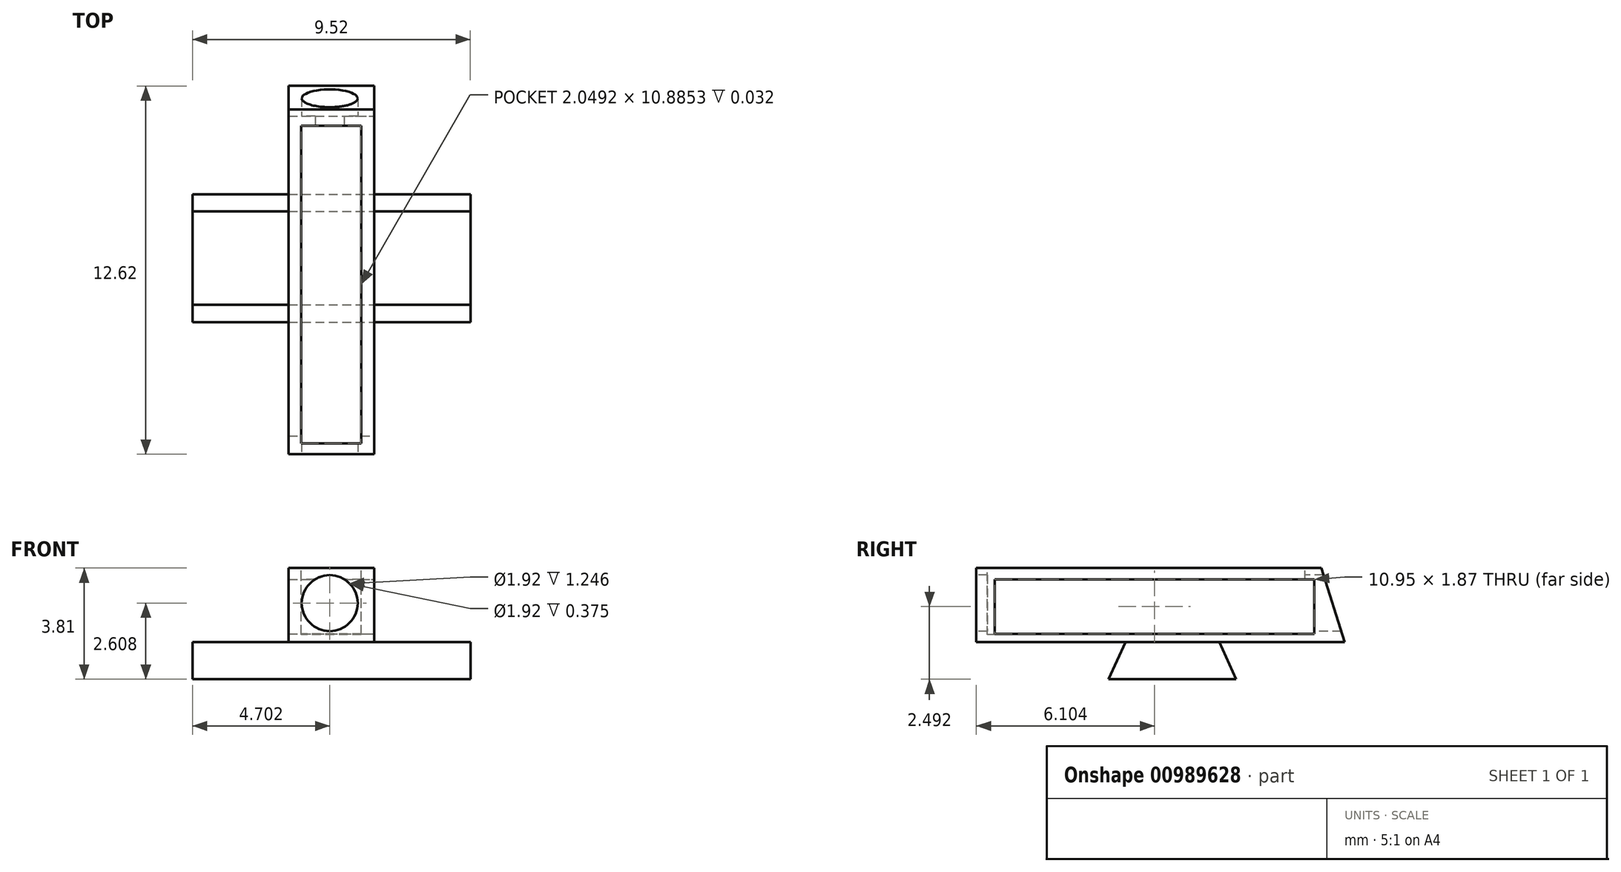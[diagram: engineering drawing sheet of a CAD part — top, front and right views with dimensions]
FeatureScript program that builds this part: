
annotation { "Feature Type Name" : "Feature", "Feature Type Description" : "" }
export const myFeature = defineFeature(function(context is Context, id is Id, definition is map)
    precondition{}
    {
        {
            var Q0;
            Q0=qCreatedBy(makeId("Top.planeOp"),FACE);
            var sketch = newSketch(context, id + "F0", { "sketchPlane" : qUnion([Q0])});
            skLineSegment(sketch, "E0.bottom", {"start": v(-27.98, 8.9) * mm, "end": v(-18.46, 8.9) * mm});
            skLineSegment(sketch, "E0.top", {"start": v(-27.98, 4.52) * mm, "end": v(-18.46, 4.52) * mm});
            skLineSegment(sketch, "E0.left", {"start": v(-27.98, 8.9) * mm, "end": v(-27.98, 4.52) * mm});
            skLineSegment(sketch, "E0.right", {"start": v(-18.46, 8.9) * mm, "end": v(-18.46, 4.52) * mm});
            skSolve(sketch);
        }
        {
            var Q0;
            Q0 = qSketchRegion(id + "F0", true);
            extrude(context, id + "F1", {"entities" : qUnion([Q0]), "depth" : 1.27 * mm, "offsetDistance" : 25.4 * mm});
        }
        {
            var Q0;
            Q0=makeQuery(id+"F1.opExtrude","CAP_FACE",FACE,{"disambiguationData":[OSD([sQuery(id+"F0.wireOp",EDGE,"E0.bottom"),sQuery(id+"F0.wireOp",EDGE,"E0.top"),sQuery(id+"F0.wireOp",EDGE,"E0.left"),sQuery(id+"F0.wireOp",EDGE,"E0.right")])],"isStart":false});
            var sketch = newSketch(context, id + "F2", { "sketchPlane" : qUnion([Q0])});
            skLineSegment(sketch, "E1.bottom", {"start": v(-21.75, 0) * mm, "end": v(-24.69, 0) * mm});
            skLineSegment(sketch, "E1.top", {"start": v(-21.75, 12.62) * mm, "end": v(-24.69, 12.62) * mm});
            skLineSegment(sketch, "E1.left", {"start": v(-21.75, 0) * mm, "end": v(-21.75, 12.62) * mm});
            skLineSegment(sketch, "E1.right", {"start": v(-24.69, 0) * mm, "end": v(-24.69, 12.62) * mm});
            skSolve(sketch);
        }
        {
            var Q0;
            Q0 = qSketchRegion(id + "F2", true);
            extrude(context, id + "F3", {"entities" : qUnion([Q0]), "operationType" : NewBodyOperationType.ADD, "depth" : 2.54 * mm, "offsetDistance" : 25.4 * mm});
        }
        {
            var Q0;
            Q0=makeQuery(id+"F3.opExtrude","SWEPT_FACE",FACE,{"disambiguationData":[OSD([sQuery(id+"F2.wireOp",EDGE,"E1.bottom")])]});
            var sketch = newSketch(context, id + "F4", { "sketchPlane" : qUnion([Q0])});
            skSolve(sketch);
        }
        {
            var Q0;
            Q0=makeQuery(id+"F1.opExtrude","SWEPT_FACE",FACE,{"disambiguationData":[OSD([sQuery(id+"F0.wireOp",EDGE,"E0.right")])]});
            var sketch = newSketch(context, id + "F5", { "sketchPlane" : qUnion([Q0])});
            skLineSegment(sketch, "E2", {"start": v(8.9, 0) * mm, "end": v(8.32, 1.27) * mm});
            skLineSegment(sketch, "E3", {"start": v(4.52, 0) * mm, "end": v(5.12, 1.27) * mm});
            skSolve(sketch);
        }
        {
            var Q0;
            {var subQ0=sQuery(id+"F5.wireOp",EDGE,"E3");Q0=makeQuery(id+"F5.imprint","IMPRINT",FACE,{"disambiguationData":[TD([[makeQuery(id+"F5.imprint","IMPRINT",EDGE,{"derivedFrom":subQ0}),1.0]])]});}
            var Q1;
            {var subQ0=sQuery(id+"F5.wireOp",EDGE,"E2");Q1=makeQuery(id+"F5.imprint","IMPRINT",FACE,{"disambiguationData":[TD([[makeQuery(id+"F5.imprint","IMPRINT",EDGE,{"derivedFrom":subQ0}),-1.0]])]});}
            extrude(context, id + "F6", {"entities" : qUnion([Q0, Q1]), "operationType" : NewBodyOperationType.REMOVE, "oppositeDirection" : true, "depth" : 25.4 * mm, "offsetDistance" : 25.4 * mm});
        }
        {
            var Q0;
            Q0=makeQuery(id+"F3.opExtrude","SWEPT_FACE",FACE,{"disambiguationData":[OSD([sQuery(id+"F2.wireOp",EDGE,"E1.left")])]});
            var sketch = newSketch(context, id + "F7", { "sketchPlane" : qUnion([Q0])});
            skLineSegment(sketch, "E4", {"start": v(12.62, 1.27) * mm, "end": v(11.82, 3.81) * mm});
            skLineSegment(sketch, "E5.bottom", {"start": v(1.04, 3.3) * mm, "end": v(11.61, 3.3) * mm});
            skLineSegment(sketch, "E5.top", {"start": v(1.04, 1.8) * mm, "end": v(11.61, 1.8) * mm});
            skLineSegment(sketch, "E5.left", {"start": v(1.04, 3.3) * mm, "end": v(1.04, 1.8) * mm});
            skLineSegment(sketch, "E5.right", {"start": v(11.61, 3.3) * mm, "end": v(11.61, 1.8) * mm});
            skSolve(sketch);
        }
        {
            var Q0;
            {var subQ0=sQuery(id+"F7.wireOp",EDGE,"E4");Q0=makeQuery(id+"F7.imprint","IMPRINT",FACE,{"disambiguationData":[TD([[makeQuery(id+"F7.imprint","IMPRINT",EDGE,{"derivedFrom":subQ0}),-1.0]])]});}
            extrude(context, id + "F8", {"entities" : qUnion([Q0]), "operationType" : NewBodyOperationType.REMOVE, "oppositeDirection" : true, "depth" : 25.4 * mm, "offsetDistance" : 25.4 * mm});
        }
        {
            var Q0;
            {var subQ0=sQuery(id+"F2.wireOp",EDGE,"E1.bottom");Q0=makeQuery(id+"F4.imprint","IMPRINT",FACE,{"disambiguationData":[TD([[makeQuery(id+"F4.imprint","IMPRINT",EDGE,{"derivedFrom":makeQuery(id+"F3.opExtrude","CAP_EDGE",EDGE,{"disambiguationData":[OSD([subQ0])],"isStart":true})}),-1.0]])]});}
            var sketch = newSketch(context, id + "F9", { "sketchPlane" : qUnion([Q0])});
            skCircle(sketch, "E6", {"center": v(-23.28, 2.6) * mm, "radius": 0.96 * mm});
            skSolve(sketch);
        }
        {
            var Q0;
            Q0=makeQuery(id+"F9.imprint","IMPRINT",FACE,{"disambiguationData":[TD([[makeQuery(id+"F9.imprint","IMPRINT",EDGE,{"derivedFrom":sQuery(id+"F9.wireOp",EDGE,"E6")}),1.0]])]});
            extrude(context, id + "F10", {"entities" : qUnion([Q0]), "operationType" : NewBodyOperationType.REMOVE, "oppositeDirection" : true, "depth" : 25.4 * mm, "offsetDistance" : 25.4 * mm});
        }
        {
            var Q0;
            Q0=makeQuery(id+"F3.opExtrude","CAP_FACE",FACE,{"disambiguationData":[OSD([sQuery(id+"F2.wireOp",EDGE,"E1.bottom"),sQuery(id+"F2.wireOp",EDGE,"E1.top"),sQuery(id+"F2.wireOp",EDGE,"E1.left"),sQuery(id+"F2.wireOp",EDGE,"E1.right")])],"isStart":false});
            var sketch = newSketch(context, id + "F11", { "sketchPlane" : qUnion([Q0])});
            skLineSegment(sketch, "E7.bottom", {"start": v(-22.2, 11.26) * mm, "end": v(-24.25, 11.26) * mm});
            skLineSegment(sketch, "E7.top", {"start": v(-22.2, 0.37) * mm, "end": v(-24.25, 0.37) * mm});
            skLineSegment(sketch, "E7.left", {"start": v(-22.2, 11.26) * mm, "end": v(-22.2, 0.37) * mm});
            skLineSegment(sketch, "E7.right", {"start": v(-24.25, 11.26) * mm, "end": v(-24.25, 0.37) * mm});
            skSolve(sketch);
        }
        {
            var Q0;
            Q0=makeQuery(id+"F11.imprint","IMPRINT",FACE,{"disambiguationData":[TD([[makeQuery(id+"F11.imprint","IMPRINT",EDGE,{"derivedFrom":sQuery(id+"F11.wireOp",EDGE,"E7.bottom")}),1.0]])]});
            extrude(context, id + "F12", {"entities" : qUnion([Q0]), "operationType" : NewBodyOperationType.REMOVE, "oppositeDirection" : true, "depth" : 2.3 * mm, "offsetDistance" : 25.4 * mm});
        }
        {
            var Q0;
            Q0=makeQuery(id+"F3.opExtrude","SWEPT_FACE",FACE,{"disambiguationData":[OSD([sQuery(id+"F2.wireOp",EDGE,"E1.left")])]});
            var sketch = newSketch(context, id + "F13", { "sketchPlane" : qUnion([Q0])});
            skLineSegment(sketch, "E8.bottom", {"start": v(0.63, 3.43) * mm, "end": v(11.58, 3.43) * mm});
            skLineSegment(sketch, "E8.top", {"start": v(0.63, 1.56) * mm, "end": v(11.58, 1.56) * mm});
            skLineSegment(sketch, "E8.left", {"start": v(0.63, 3.43) * mm, "end": v(0.63, 1.56) * mm});
            skLineSegment(sketch, "E8.right", {"start": v(11.58, 3.43) * mm, "end": v(11.58, 1.56) * mm});
            skSolve(sketch);
        }
        {
            var Q0;
            Q0 = qSketchRegion(id + "F13", true);
            extrude(context, id + "F14", {"entities" : qUnion([Q0]), "operationType" : NewBodyOperationType.REMOVE, "oppositeDirection" : true, "depth" : 25.4 * mm, "offsetDistance" : 25.4 * mm});
        }
    });
